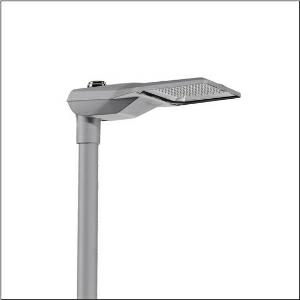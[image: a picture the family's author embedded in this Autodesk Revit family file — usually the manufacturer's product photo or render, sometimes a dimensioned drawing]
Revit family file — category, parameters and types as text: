
# Revit family: streetlight_sl_21_midi___st1_5a_5xe7p37n08mb_d4f4
name_source: partatom
category: Lighting Fixtures
units: mm (PartAtom-declared; Revit-internal decimal feet)

## family parameters
Cut with Voids When Loaded = No
Host = Face
Light Source = No
Part Type = Normal
Room Calculation Point = No
Round Connector Dimension = Use Diameter
Shared = No

## types (1)
- --- (1 x LED, 17960 lm, 136 W, 3000K)
    Apparent Load = 136 VA
    CIE Flux Codes = 22 53 95 100 100
    Color Rendering = 70
    Color Temperature = 3000K
    Default Elevation = 1800 mm
    Description = Streetlight SL 21 midi, mast luminaire, primary light control with lens, of PMMA, primary optical cover: cover, of toughened safety glass, transparent, light distribution: ST1.5a, light emission: direct distribution, primary light characteristic: asymmetric, installation type: side-entry, LED, 3G 2.5mm², High Power LED, rated luminous flux: 17.960lm, luminous efficacy: 132lm/W, light colour: 730, colour temperature: 3000K, control gear: NEMA (7pin), control: overheat protection, pre-setting: linear dimming characteristic, constant luminous flux control, time-dependent luminous flux control, flexible luminous flux parameterisation, mains connection: 220..240V, AC, 50/60Hz, connection cable pre-assembled, cable length: 12,5m, wiring characteristics: H05VV-F, start of lifetime: 136W, end of service life: 142W, reduction: 61W, luminaire housing, of diecast aluminium (EN AC-44300), powder-coated, Siteco® metallic grey (DB 702S), corrosivity category C5 mid according to DIN EN ISO 12944, multi-level sealing system, sealing non-destructively replaceable, inclination adjustable: 0°, 5°, 10°, 15°, length: 644mm, width: 335mm, height: 110mm, spigot size: 42mm (side-entry), mounting height: 4..8m, protection rating (complete): IP66, insulation class (complete): insulation class I (protective earthing), certification: CE, ENEC, ENEC+, VDE, impact resistance: IK10, permissible operating ambient temperature for outdoor applications: -40..+50°C, standard-compliant lighting for roads and squares, packaging unit: 1 piece

Light Distribution: ST1.5a
    Height = 111 mm
    Lamp = 1 x LED
    Lamp Light Flux = 17960 lm
    Lamp Power = 136 W
    Lamp count = 1
    Length = 644 mm
    Luminous efficacy = 132 lm/W
    Manufacturer = Siteco
    ModVariant = No
    Model = 5XE7P37N08MB
    Number of Poles = 1
    OnlyDefault = Yes
    Power Factor = 1
    Product Name = Streetlight SL 21 midi | ST1.5a
    Product group = mast luminaire | pylon top
    ProductGroupID = 6100
    Protection Class = Protection class I
    Protection Degree = IP 66
    RLX_Detail_Level = 1
    RLX_Emergency_Light_Flux = 0 lm
    RLX_Emergency_Type = 0
    RLX_Emergency_Type_DB = No
    RlxData = <blob elided: 30057 chars, md5=8df4e76e>
    Socket = socket
    Standby Power = 0 W
    System Light Flux = 17960 lm
    System Power = 136 W
    Type Comments = factory setting: luminous flux: 100 % | dim-lin: 254 | 695 mA
    Type Image = l_1294377.jpg
    URL = http://relux.com
    VarID = @adj_154941
    Voltage = 0 V
    Weight = 0.00 kg
    Width = 336 mm

## geometry (parser evidence)
native form markers: Blend x4, Sweep x11
no freeform markers — native parametric forms only
